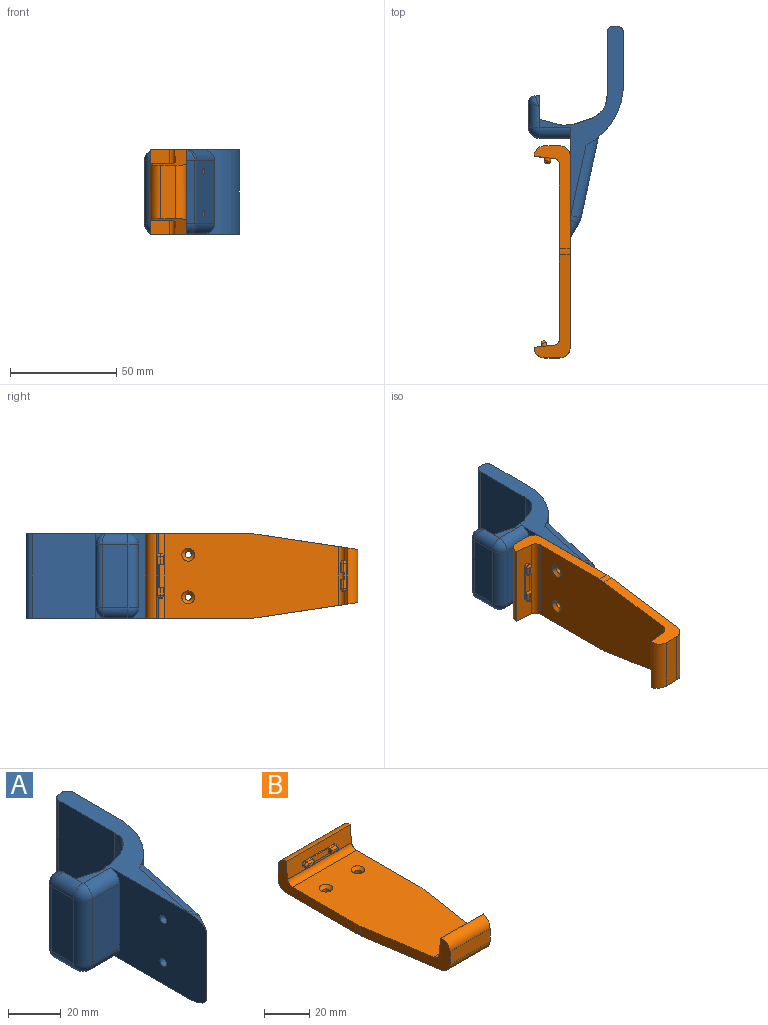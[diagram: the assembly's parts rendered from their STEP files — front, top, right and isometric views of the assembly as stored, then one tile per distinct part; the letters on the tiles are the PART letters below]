
ASSEMBLY  parts=2 mates=1
PART A: 37 faces, bbox 44.8x100x40.1 mm
  f0: plane 30x2mm, normal (0,1,0), area 60mm2, adj f1,f16,f25,f30
  f1: cylinder r=3mm len=30mm, axis (0,0,-1), area 141.4mm2, adj f0,f2,f24,f29
  f2: plane 30x12mm, normal (-1,0,0), area 360mm2, adj f1,f3,f23,f28
  f3: cylinder r=5mm len=30mm, axis (0,0,-1), area 235.6mm2, adj f2,f4,f22,f27
  f4: plane 30x14.62mm, normal (0,-1,0), area 438.7mm2, adj f3,f5,f21,f26
  f5: plane 52.07x40.07mm, normal (-1,0,0), area 1850.6mm2, adj f4,f6,f17,f18,f19,f20,f21,f26
  f6: plane 30x6.47mm, normal (0.86,-0.51,0), area 226.1mm2, adj f5,f7,f33,f36
  f7: cylinder r=10mm len=30mm, axis (0,0,-1), area 97.6mm2, adj f6,f8,f32,f35
  f8: plane 38.2x30mm, normal (0.98,-0.21,0), area 1153.1mm2, adj f7,f9,f19,f20,f31,f34
  f9: cylinder r=31.97mm len=40mm, axis (0,0,-1), area 1145.6mm2, adj f8,f10,f17,f18,f31,f34
  f10: plane 40x24.53mm, normal (1,0,0), area 981.4mm2, adj f9,f11,f17,f18
  f11: cylinder r=3mm len=40mm, axis (0,0,-1), area 188.5mm2, adj f10,f12,f17,f18
  f12: plane 40x1.69mm, normal (0,1,0), area 67.4mm2, adj f11,f13,f17,f18
  f13: cylinder r=3mm len=40mm, axis (0,0,-1), area 188.5mm2, adj f12,f14,f17,f18
  f14: plane 40x29.91mm, normal (-1,0,0), area 1196.5mm2, adj f13,f15,f17,f18
  f15: extruded ~40x32mm, area 1576.7mm2, adj f14,f16,f17,f18
  f16: plane 40x11mm, normal (1,0,0), area 429.3mm2, adj f0,f15,f23,f25,f28,f30
  f17: plane 90x39.69mm, normal (0,0,1), area 662.9mm2, adj f5,f9,f10,f11,f12,f13,f14,f15
  f18: plane 90x39.69mm, normal (0,0,-1), area 662.9mm2, adj f5,f9,f10,f11,f12,f13,f14,f15
  f19: cylinder r=1.75mm len=8.51mm, axis (-1,0,0), area 89.3mm2, adj f5,f8
  f20: cylinder r=1.75mm len=8.51mm, axis (-1,0,0), area 89.3mm2, adj f5,f8
  f21: cylinder r=5mm len=14.62mm, axis (1,0,0), area 114.8mm2, adj f4,f5,f18,f22
  f22: sphere r=5mm, area 39.3mm2, adj f3,f21,f23
  f23: cylinder r=5mm len=12mm, axis (0,-1,0), area 86.4mm2, adj f2,f16,f18,f22,f24
  f24: bspline ~6.03x5mm, area 24.5mm2, adj f1,f23,f25
  f25: cylinder r=5mm len=5mm, axis (-1,0,0), area 7.9mm2, adj f0,f16,f24
  f26: cylinder r=5mm len=14.62mm, axis (-1,0,0), area 114.8mm2, adj f4,f5,f17,f27
  f27: sphere r=5mm, area 39.3mm2, adj f3,f26,f28
  f28: cylinder r=5mm len=12mm, axis (0,1,0), area 86.4mm2, adj f2,f16,f17,f27,f29
  f29: bspline ~6.03x5mm, area 24.5mm2, adj f1,f28,f30
  f30: cylinder r=5mm len=5mm, axis (1,0,0), area 7.9mm2, adj f0,f16,f29
  f31: cylinder r=5mm len=39.26mm, axis (0.21,0.98,0), area 291.4mm2, adj f8,f9,f18,f32
  f32: torus R=5mm, axis (0,0,1), area 20.7mm2, adj f5,f7,f18,f31,f33
  f33: cylinder r=5mm len=8.79mm, axis (0.51,0.86,0), area 35.6mm2, adj f5,f6,f32
  f34: cylinder r=5mm len=39.26mm, axis (-0.21,-0.98,0), area 291.4mm2, adj f8,f9,f17,f35
  f35: torus R=5mm, axis (0,0,1), area 20.7mm2, adj f5,f7,f17,f34,f36
  f36: cylinder r=5mm len=8.79mm, axis (-0.51,-0.86,0), area 35.6mm2, adj f5,f6,f35
PART B: 54 faces, bbox 40x100x17 mm
  f0: plane 4.75x0.5mm, normal (0,0.99,0.11), area 2.3mm2, adj f36,f37,f39,f48
  f1: cylinder r=1mm len=4.5mm, axis (-1,0,0), area 7.1mm2, adj f34,f35,f38,f49
  f2: cylinder r=1mm len=4.5mm, axis (1,0,0), area 7.1mm2, adj f32,f35,f38,f49
  f3: plane 4.04x0.99mm, normal (0,-0.99,0.11), area 3.9mm2, adj f27,f28,f30,f45
  f4: cylinder r=1mm len=3.46mm, axis (1,0,0), area 5.4mm2, adj f22,f26,f29,f46
  f5: cylinder r=1mm len=3.46mm, axis (-1,0,0), area 5.4mm2, adj f24,f26,f29,f46
  f6: cylinder r=20.06mm len=5.07mm, axis (0,0,-1), area 15.1mm2, adj f7,f12,f16,f18
  f7: plane 48.52x17mm, normal (-0.99,-0.15,0), area 307.7mm2, adj f6,f11,f13,f16,f17,f18,f19,f40
  f8: plane 48.52x17mm, normal (0.99,-0.15,0), area 307.7mm2, adj f9,f11,f13,f16,f17,f18,f19,f40
  f9: cylinder r=20.06mm len=5.07mm, axis (0,0,-1), area 15.1mm2, adj f8,f10,f16,f18
  f10: plane 48.5x17mm, normal (1,0,0), area 304.2mm2, adj f9,f14,f15,f16,f18,f20,f21,f41
  f11: plane 26.5x0.01mm, normal (0,0,1), area 0.2mm2, adj f7,f8,f19,f42
  f12: plane 48.5x17mm, normal (-1,0,0), area 304.2mm2, adj f6,f14,f15,f16,f18,f20,f21,f41
  f13: plane 25x7mm, normal (0,-1,0), area 175mm2, adj f7,f8,f40,f42
  f14: plane 40x7mm, normal (0,1,0), area 280mm2, adj f10,f12,f41,f43
  f15: plane 40x0.01mm, normal (0,0,1), area 0.3mm2, adj f10,f12,f20,f43
  f16: plane 90x40mm, normal (0,0,-1), area 3282mm2, adj f6,f7,f8,f9,f10,f12,f40,f41
  f17: cylinder r=3mm len=27.7mm, axis (-1,0,0), area 119.1mm2, adj f7,f8,f18,f19
  f18: plane 82x40mm, normal (0,0,1), area 2971.2mm2, adj f6,f7,f8,f9,f10,f12,f17,f21
  f19: plane 26.81x9.25mm, normal (0,0.99,0.11), area 213.2mm2, adj f7,f8,f11,f17,f31,f32,f33,f34
  f20: plane 40x9.25mm, normal (0,-0.99,0.11), area 311.4mm2, adj f10,f12,f15,f21,f22,f23,f24,f25
  f21: cylinder r=3mm len=40mm, axis (-1,0,0), area 175.5mm2, adj f10,f12,f18,f20
  f22: plane 18x1.49mm, normal (0,0.11,0.99), area 16mm2, adj f4,f20,f23,f25,f27,f44,f45,f46
  f23: cylinder r=1.5mm len=3.15mm, axis (0,0.99,-0.11), area 7.3mm2, adj f20,f22,f24,f28
  f24: plane 17.85x1.49mm, normal (0,-0.11,-0.99), area 15.8mm2, adj f5,f20,f23,f25,f30,f44,f45,f46
  f25: cylinder r=1.5mm len=3.15mm, axis (0,0.99,-0.11), area 7.1mm2, adj f20,f22,f24,f29
  f26: plane 3.96x0.99mm, normal (0,-0.99,0.11), area 3.8mm2, adj f4,f5,f29,f46
  f27: cylinder r=1mm len=3.54mm, axis (1,0,0), area 5.6mm2, adj f3,f22,f28,f45
  f28: torus R=0.5mm, axis (0,0.99,-0.11), area 5.8mm2, adj f3,f23,f27,f30
  f29: torus R=0.5mm, axis (0,0.99,-0.11), area 5.6mm2, adj f4,f5,f25,f26
  f30: cylinder r=1mm len=3.46mm, axis (-1,0,0), area 5.4mm2, adj f3,f24,f28,f45
  f31: cylinder r=1.25mm len=2.65mm, axis (0,-0.99,-0.11), area 5.9mm2, adj f19,f32,f34,f37
  f32: plane 12x1.49mm, normal (0,0.11,-0.99), area 16.5mm2, adj f2,f19,f31,f33,f39,f47,f48,f49
  f33: cylinder r=1.25mm len=2.65mm, axis (0,-0.99,-0.11), area 5.9mm2, adj f19,f32,f34,f38
  f34: plane 12x1.49mm, normal (0,-0.11,0.99), area 16.5mm2, adj f1,f19,f31,f33,f36,f47,f48,f49
  f35: plane 4.75x0.5mm, normal (0,0.99,0.11), area 2.3mm2, adj f1,f2,f38,f49
  f36: cylinder r=1mm len=4.5mm, axis (-1,0,0), area 7.1mm2, adj f0,f34,f37,f48
  f37: torus R=0.25mm, axis (0,-0.99,-0.11), area 4.4mm2, adj f0,f31,f36,f39
  f38: torus R=0.25mm, axis (0,-0.99,-0.11), area 4.4mm2, adj f1,f2,f33,f35
  f39: cylinder r=1mm len=4.5mm, axis (1,0,0), area 7.1mm2, adj f0,f32,f37,f48
  f40: cylinder r=5mm len=26.5mm, axis (1,0,0), area 200.6mm2, adj f7,f8,f13,f16
  f41: cylinder r=5mm len=40mm, axis (-1,0,0), area 314.2mm2, adj f10,f12,f14,f16
  f42: cylinder r=5mm len=26.5mm, axis (-1,0,0), area 200.6mm2, adj f7,f8,f11,f13
  f43: cylinder r=5mm len=40mm, axis (1,0,0), area 314.2mm2, adj f10,f12,f14,f15
  f44: plane 11x2.98mm, normal (0,-0.99,0.11), area 33mm2, adj f22,f24,f45,f46
  f45: plane 3.09x2.21mm, normal (-1,0,0), area 5.6mm2, adj f3,f22,f24,f27,f30,f44
  f46: plane 3.1x2.21mm, normal (1,0,0), area 5.6mm2, adj f4,f5,f22,f24,f26,f44
  f47: plane 3x2.49mm, normal (0,0.99,0.11), area 7.5mm2, adj f32,f34,f48,f49
  f48: plane 2.55x1.66mm, normal (1,0,0), area 3.3mm2, adj f0,f32,f34,f36,f39,f47
  f49: plane 2.55x1.66mm, normal (-1,0,0), area 3.3mm2, adj f1,f2,f32,f34,f35,f47
  f50: cylinder r=1.5mm len=3.57mm, axis (0,0,-1), area 33.7mm2, adj f16,f52
  f51: cylinder r=1.5mm len=3.57mm, axis (0,0,-1), area 33.7mm2, adj f16,f53
  f52: cone r=3mm half-angle=45deg, axis (0,0,1), area 30mm2, adj f18,f50
  f53: cone r=3mm half-angle=45deg, axis (0,0,1), area 30mm2, adj f18,f51
PLACE A at identity fixed
PLACE B rot(axis=(0,-1,0),90deg) t=(-20,-6.5,20)mm
MATE fastened B.f53 <-> A.f20  axis (1,0,0) through (-20,23.5,30)mm
